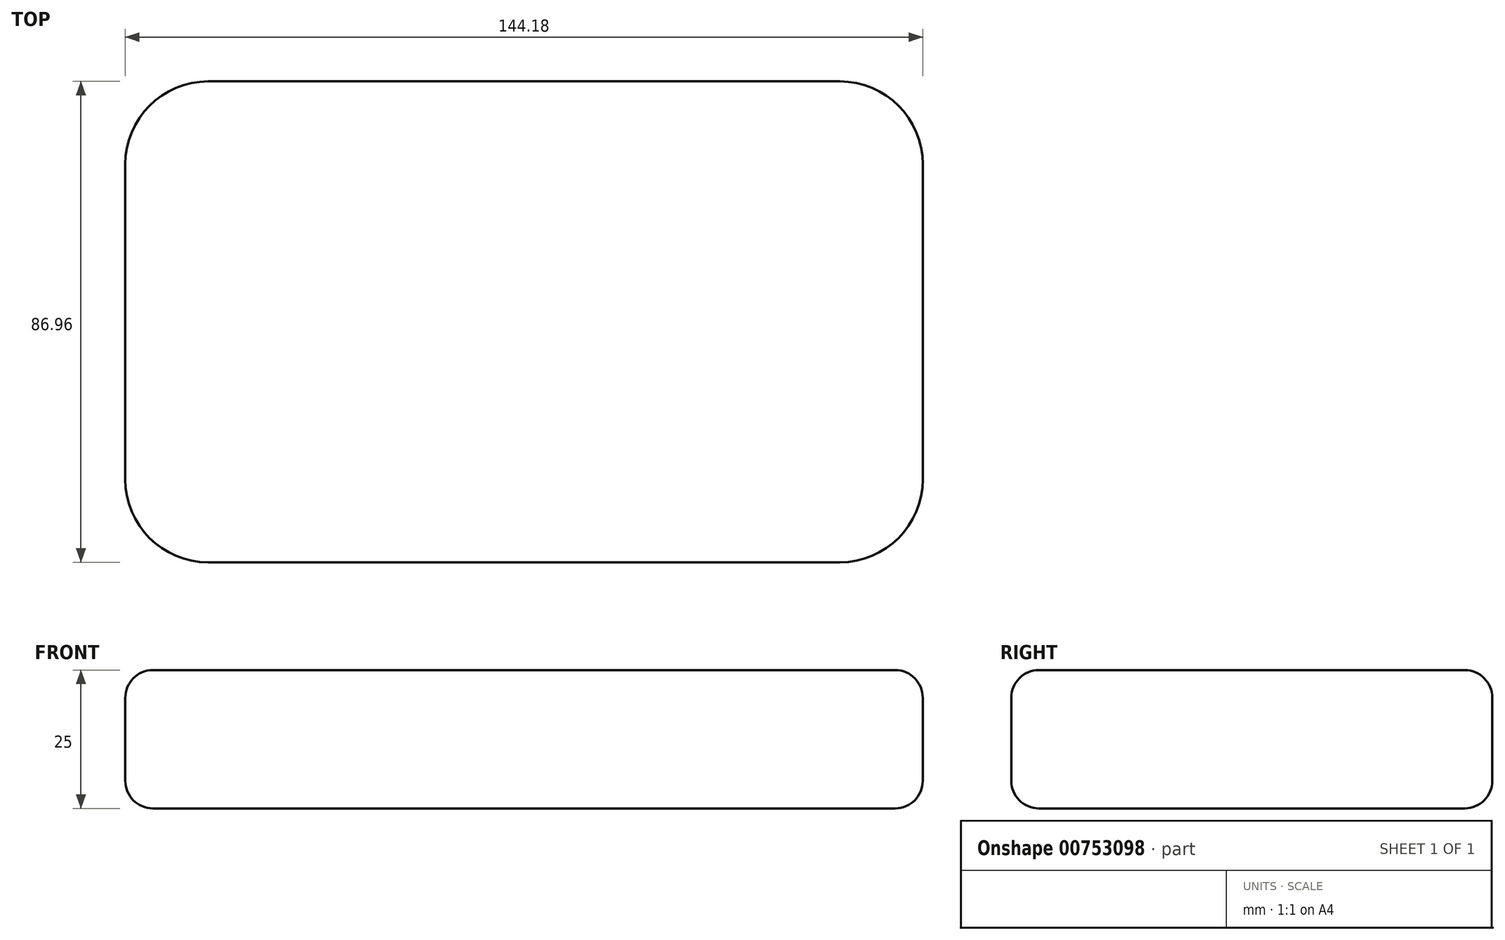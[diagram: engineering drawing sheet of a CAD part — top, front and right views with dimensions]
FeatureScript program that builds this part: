
annotation { "Feature Type Name" : "Feature", "Feature Type Description" : "" }
export const myFeature = defineFeature(function(context is Context, id is Id, definition is map)
    precondition{}
    {
        {
            var Q0;
            Q0=qCreatedBy(makeId("Top.planeOp"),FACE);
            var sketch = newSketch(context, id + "F0", { "sketchPlane" : qUnion([Q0])});
            skLineSegment(sketch, "E0.bottom", {"start": v(-72.1, -43.48) * mm, "end": v(72.1, -43.48) * mm});
            skLineSegment(sketch, "E0.top", {"start": v(-72.1, 43.48) * mm, "end": v(72.1, 43.48) * mm});
            skLineSegment(sketch, "E0.left", {"start": v(-72.1, -43.48) * mm, "end": v(-72.1, 43.48) * mm});
            skLineSegment(sketch, "E0.right", {"start": v(72.1, -43.48) * mm, "end": v(72.1, 43.48) * mm});
            skPoint(sketch, "E0.middle", {"position": v(0, 0) * mm});
            skSolve(sketch);
        }
        {
            var Q0;
            Q0 = qSketchRegion(id + "F0", true);
            extrude(context, id + "F1", {"entities" : qUnion([Q0]), "depth" : 25 * mm, "offsetDistance" : 25 * mm});
        }
        {
            var Q0;
            Q0=makeQuery(id+"F1.opExtrude","SWEPT_EDGE",EDGE,{"disambiguationData":[OSD([sQuery(id+"F0.wireOp",EDGE,"E0.top"),sQuery(id+"F0.wireOp",EDGE,"E0.right")])]});
            var Q1;
            Q1=makeQuery(id+"F1.opExtrude","SWEPT_EDGE",EDGE,{"disambiguationData":[OSD([sQuery(id+"F0.wireOp",EDGE,"E0.bottom"),sQuery(id+"F0.wireOp",EDGE,"E0.right")])]});
            var Q2;
            Q2=makeQuery(id+"F1.opExtrude","SWEPT_EDGE",EDGE,{"disambiguationData":[OSD([sQuery(id+"F0.wireOp",EDGE,"E0.top"),sQuery(id+"F0.wireOp",EDGE,"E0.left")])]});
            var Q3;
            Q3=makeQuery(id+"F1.opExtrude","SWEPT_EDGE",EDGE,{"disambiguationData":[OSD([sQuery(id+"F0.wireOp",EDGE,"E0.bottom"),sQuery(id+"F0.wireOp",EDGE,"E0.left")])]});
            fillet(context, id + "F2", {"entities" : qUnion([Q0, Q1, Q2, Q3]), "radius" : 15 * mm, "tangentPropagation" : true, "allowEdgeOverflow" : false});
        }
        {
            var Q0;
            Q0=makeQuery(id+"F1.opExtrude","CAP_FACE",FACE,{"disambiguationData":[OSD([sQuery(id+"F0.wireOp",EDGE,"E0.bottom"),sQuery(id+"F0.wireOp",EDGE,"E0.top"),sQuery(id+"F0.wireOp",EDGE,"E0.left"),sQuery(id+"F0.wireOp",EDGE,"E0.right")])],"isStart":false});
            var Q1;
            Q1=makeQuery(id+"F1.opExtrude","CAP_FACE",FACE,{"disambiguationData":[OSD([sQuery(id+"F0.wireOp",EDGE,"E0.bottom"),sQuery(id+"F0.wireOp",EDGE,"E0.top"),sQuery(id+"F0.wireOp",EDGE,"E0.left"),sQuery(id+"F0.wireOp",EDGE,"E0.right")])],"isStart":true});
            fillet(context, id + "F3", {"entities" : qUnion([Q0, Q1]), "radius" : 5 * mm, "tangentPropagation" : true, "allowEdgeOverflow" : false});
        }
    });
